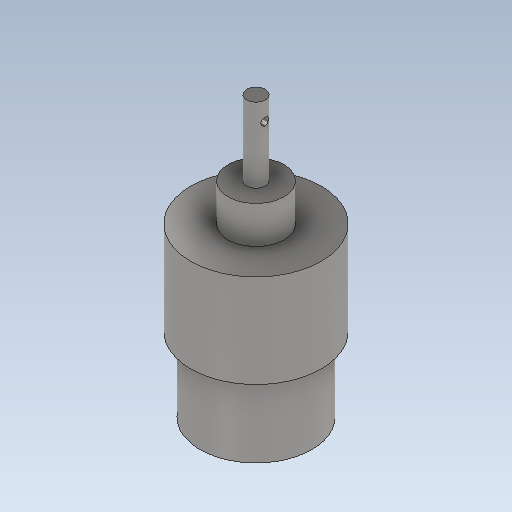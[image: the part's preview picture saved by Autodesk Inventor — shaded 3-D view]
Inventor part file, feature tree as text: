
AUTODESK INVENTOR PART (.ipt)
format: ipt  version: 2020.2 (Build 242310000, 310)  size: 134,144 bytes
history: native  units: in
note: dims shown in document units (in); Inventor stores cm internally (conversion verified against a paired STEP export)
features: extrude x5, sketch x5
ambient origin geometry x8: Origin, YZ Plane, XZ Plane, XY Plane, X Axis, Y Axis, Z Axis, Center Point
bodies: Solid1 (feature_tree)
feature tree (10):
  extrude  "Extrusion1"  Depth=0.7874in TaperAngle=0.0deg
  extrude  "Extrusion2"  Depth=0.9843in TaperAngle=0.0deg
  extrude  "Extrusion3"  Depth=0.3937in TaperAngle=0.0deg
  extrude  "Extrusion4"  Depth=0.7874in TaperAngle=0.0deg
  extrude  "Extrusion5"  Depth=0.3937in TaperAngle=0.0deg
  sketch  "Sketch1"  dims[d0=1.1811in d1=0.7874in d2=0.0in]
  sketch  "Sketch2"  dims[d3=1.378in d4=0.9843in d5=0.0in]
  sketch  "Sketch3"  dims[d6=0.5906in d7=0.3937in d8=0.0in]
  sketch  "Sketch4"  dims[d9=0.1969in d10=0.7874in d11=0.0in]
  sketch  "Sketch5"  dims[d12=0.0787in d13=0.3937in d14=0.0in]
